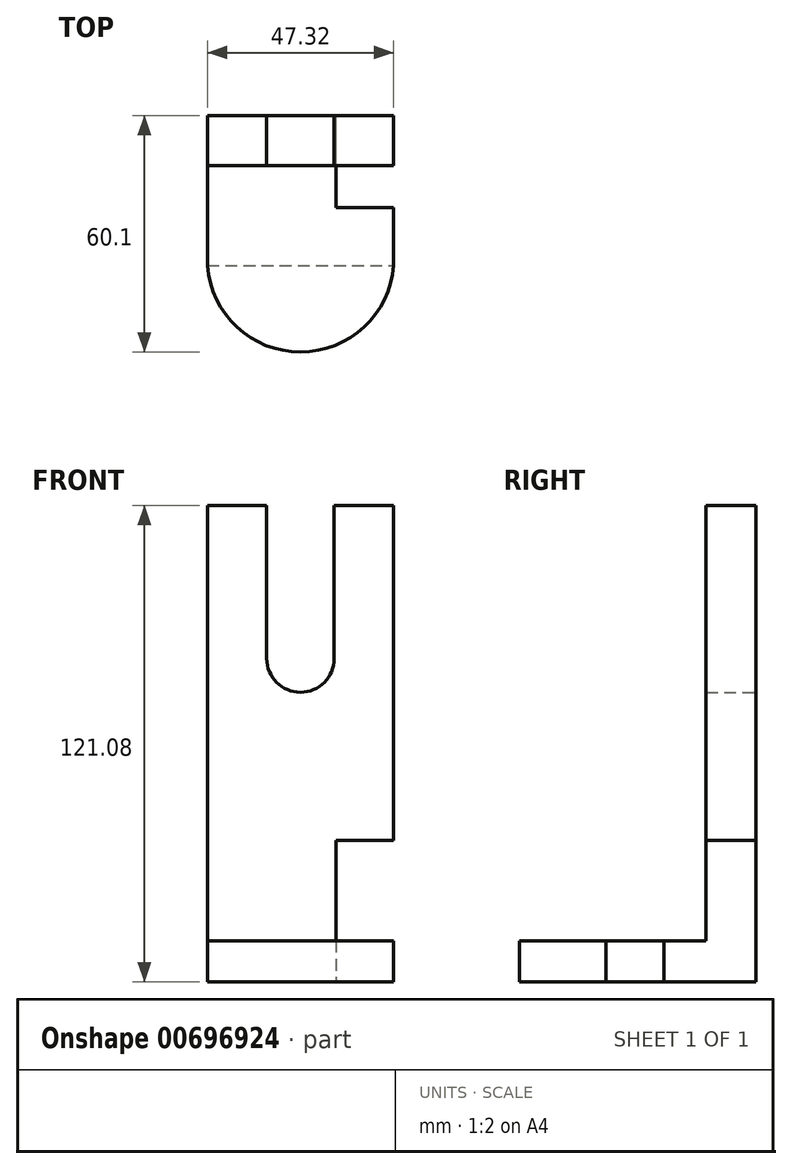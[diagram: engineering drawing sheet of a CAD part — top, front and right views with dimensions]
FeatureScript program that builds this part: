
annotation { "Feature Type Name" : "Feature", "Feature Type Description" : "" }
export const myFeature = defineFeature(function(context is Context, id is Id, definition is map)
    precondition{}
    {
        {
            var Q0;
            Q0=qCreatedBy(makeId("Front.planeOp"),FACE);
            var sketch = newSketch(context, id + "F0", { "sketchPlane" : qUnion([Q0])});
            skLineSegment(sketch, "E0.bottom", {"start": v(-23.66, 60.54) * mm, "end": v(-8.57, 60.54) * mm});
            skLineSegment(sketch, "E0.top", {"start": v(-23.66, -60.54) * mm, "end": v(23.66, -60.54) * mm});
            skLineSegment(sketch, "E0.left", {"start": v(-23.66, 60.54) * mm, "end": v(-23.66, -60.54) * mm});
            skLineSegment(sketch, "E0.right", {"start": v(23.66, 60.54) * mm, "end": v(23.66, -60.54) * mm});
            skPoint(sketch, "E0.middle", {"position": v(0, 0) * mm});
            skLineSegment(sketch, "E1.top", {"start": v(0, 21.63) * mm, "end": v(0, 21.63) * mm});
            skLineSegment(sketch, "E1.left", {"start": v(-8.57, 60.54) * mm, "end": v(-8.57, 21.63) * mm});
            skLineSegment(sketch, "E1.right", {"start": v(8.57, 60.54) * mm, "end": v(8.57, 21.63) * mm});
            skArc(sketch, "E2", {"start": v(-8.57, 21.63) * mm, "mid": v(0, 13.07) * mm, "end": v(8.57, 21.63) * mm});
            skPoint(sketch, "E2.centerSnap0", {"position": v(0, 21.63) * mm});
            skLineSegment(sketch, "E3.trimOffspring", {"start": v(8.57, 21.63) * mm, "end": v(8.57, 21.63) * mm});
            skLineSegment(sketch, "E4.trimOffspring", {"start": v(8.57, 60.54) * mm, "end": v(23.66, 60.54) * mm});
            skSolve(sketch);
        }
        {
            var Q0;
            Q0=makeQuery(id+"F0.imprint","IMPRINT",FACE,{"disambiguationData":[TD([[makeQuery(id+"F0.imprint","IMPRINT",EDGE,{"derivedFrom":sQuery(id+"F0.wireOp",EDGE,"E0.bottom")}),-1.0]])]});
            extrude(context, id + "F1", {"entities" : qUnion([Q0]), "depth" : 12.7 * mm, "offsetDistance" : 25.4 * mm});
        }
        {
            var Q0;
            Q0=makeQuery(id+"F1.opExtrude","CAP_FACE",FACE,{"disambiguationData":[OSD([sQuery(id+"F0.wireOp",EDGE,"E0.bottom"),sQuery(id+"F0.wireOp",EDGE,"E0.top"),sQuery(id+"F0.wireOp",EDGE,"E0.left"),sQuery(id+"F0.wireOp",EDGE,"E0.right"),sQuery(id+"F0.wireOp",EDGE,"E1.left"),sQuery(id+"F0.wireOp",EDGE,"E1.right"),sQuery(id+"F0.wireOp",EDGE,"E2"),sQuery(id+"F0.wireOp",EDGE,"E4.trimOffspring")])],"isStart":false});
            var sketch = newSketch(context, id + "F2", { "sketchPlane" : qUnion([Q0])});
            skLineSegment(sketch, "E5.bottom", {"start": v(-23.66, -50.04) * mm, "end": v(23.66, -50.04) * mm});
            skLineSegment(sketch, "E5.top", {"start": v(-23.66, -60.54) * mm, "end": v(23.66, -60.54) * mm});
            skLineSegment(sketch, "E5.left", {"start": v(-23.66, -50.04) * mm, "end": v(-23.66, -60.54) * mm});
            skLineSegment(sketch, "E5.right", {"start": v(23.66, -50.04) * mm, "end": v(23.66, -60.54) * mm});
            skSolve(sketch);
        }
        {
            var Q0;
            Q0 = qSketchRegion(id + "F2", true);
            extrude(context, id + "F3", {"entities" : qUnion([Q0]), "operationType" : NewBodyOperationType.ADD, "depth" : 25.4 * mm, "offsetDistance" : 25.4 * mm});
        }
        {
            var Q0;
            Q0=makeQuery(id+"F3.opExtrude","SWEPT_FACE",FACE,{"disambiguationData":[OSD([sQuery(id+"F2.wireOp",EDGE,"E5.bottom")])]});
            var sketch = newSketch(context, id + "F4", { "sketchPlane" : qUnion([Q0])});
            skArc(sketch, "E6", {"start": v(-23.66, -38.1) * mm, "mid": v(1.72, -60.04) * mm, "end": v(23.66, -34.65) * mm});
            skPoint(sketch, "E6.first.point", {"position": v(-23.66, -38.1) * mm});
            skPoint(sketch, "E6.second.point", {"position": v(23.66, -38.1) * mm});
            skPoint(sketch, "E6.third.point", {"position": v(23.66, -34.65) * mm});
            skSolve(sketch);
        }
        {
            var Q0;
            Q0 = qSketchRegion(id + "F4", true);
            var Q1;
            {var subQ1=sQuery(id+"F2.wireOp",EDGE,"E5.bottom");var subQ2=makeQuery(id+"F3.opExtrude","CAP_EDGE",EDGE,{"disambiguationData":[OSD([subQ1])],"isStart":false});Q1=makeQuery(id+"F4.imprint","IMPRINT",FACE,{"disambiguationData":[TD([[makeQuery(id+"F4.imprint","IMPRINT",EDGE,{"derivedFrom":subQ2}),-1.0]])]});}
            extrude(context, id + "F5", {"entities" : qUnion([Q0, Q1]), "operationType" : NewBodyOperationType.ADD, "oppositeDirection" : true, "depth" : 10.4 * mm, "offsetDistance" : 25.4 * mm});
        }
        {
            var Q0;
            Q0=makeQuery(id+"F1.opExtrude","CAP_FACE",FACE,{"disambiguationData":[OSD([sQuery(id+"F0.wireOp",EDGE,"E0.bottom"),sQuery(id+"F0.wireOp",EDGE,"E0.top"),sQuery(id+"F0.wireOp",EDGE,"E0.left"),sQuery(id+"F0.wireOp",EDGE,"E0.right"),sQuery(id+"F0.wireOp",EDGE,"E1.left"),sQuery(id+"F0.wireOp",EDGE,"E1.right"),sQuery(id+"F0.wireOp",EDGE,"E2"),sQuery(id+"F0.wireOp",EDGE,"E4.trimOffspring")])],"isStart":true});
            var sketch = newSketch(context, id + "F6", { "sketchPlane" : qUnion([Q0])});
            skLineSegment(sketch, "E7.bottom", {"start": v(-36.21, -24.61) * mm, "end": v(-9, -24.61) * mm});
            skLineSegment(sketch, "E7.top", {"start": v(-36.21, -65.7) * mm, "end": v(-9, -65.7) * mm});
            skLineSegment(sketch, "E7.left", {"start": v(-36.21, -24.61) * mm, "end": v(-36.21, -65.7) * mm});
            skLineSegment(sketch, "E7.right", {"start": v(-9, -24.61) * mm, "end": v(-9, -65.7) * mm});
            skSolve(sketch);
        }
        {
            var Q0;
            Q0 = qSketchRegion(id + "F6", true);
            extrude(context, id + "F7", {"entities" : qUnion([Q0]), "operationType" : NewBodyOperationType.REMOVE, "oppositeDirection" : true, "depth" : 23.37 * mm, "offsetDistance" : 25.4 * mm});
        }
    });
